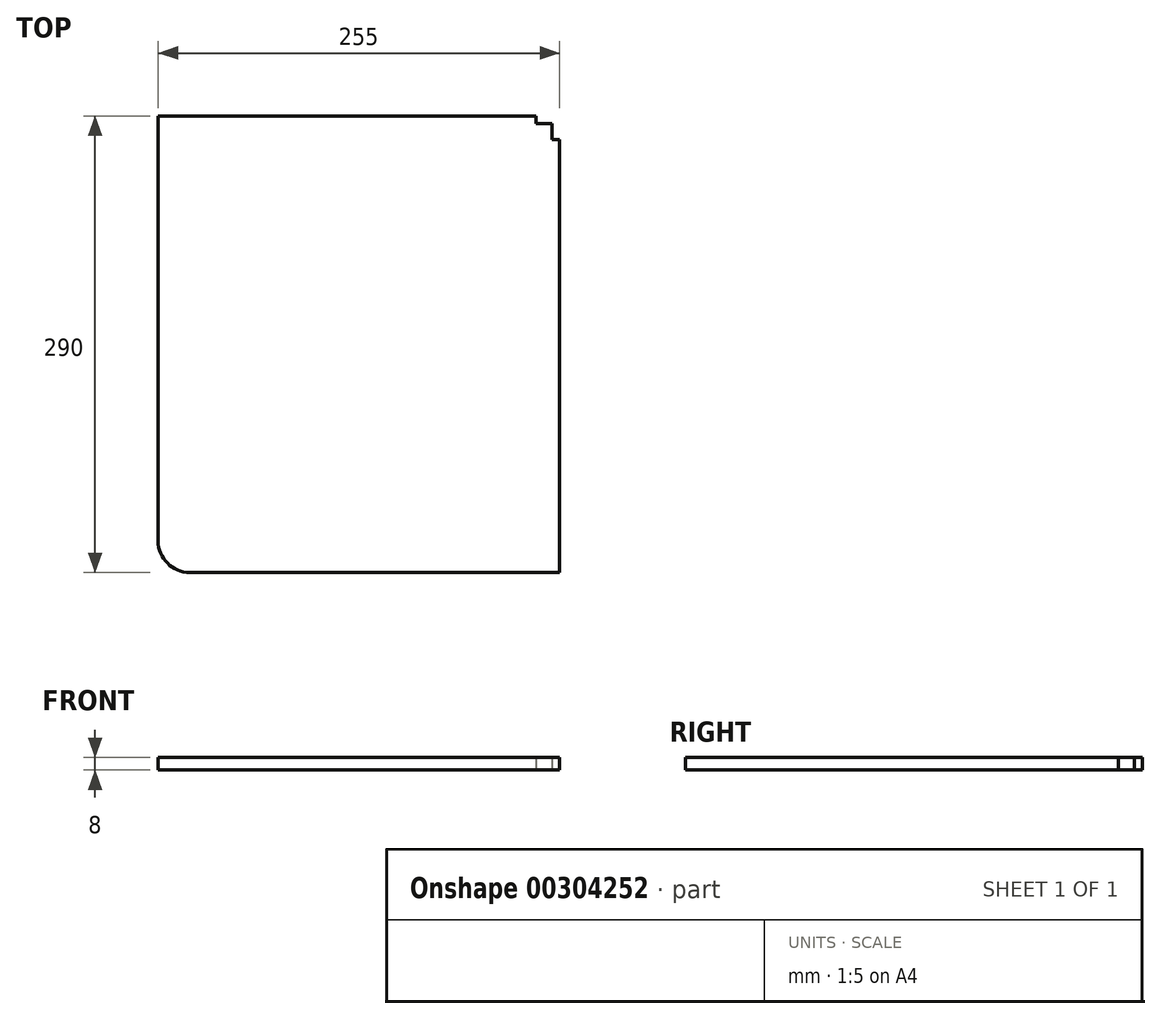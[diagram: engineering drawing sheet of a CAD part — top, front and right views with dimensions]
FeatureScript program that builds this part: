
annotation { "Feature Type Name" : "Feature", "Feature Type Description" : "" }
export const myFeature = defineFeature(function(context is Context, id is Id, definition is map)
    precondition{}
    {
        {
            var Q0;
            Q0=qCreatedBy(makeId("Top.planeOp"),FACE);
            var sketch = newSketch(context, id + "F0", { "sketchPlane" : qUnion([Q0])});
            skLineSegment(sketch, "E0", {"start": v(112.5, 145) * mm, "end": v(-127.5, 145) * mm});
            skLineSegment(sketch, "E1", {"start": v(-127.5, 145) * mm, "end": v(-127.5, -125) * mm});
            skLineSegment(sketch, "E2", {"start": v(-107.5, -145) * mm, "end": v(127.5, -145) * mm});
            skLineSegment(sketch, "E3", {"start": v(127.5, -145) * mm, "end": v(127.5, 130) * mm});
            skLineSegment(sketch, "E4", {"start": v(127.5, 130) * mm, "end": v(122.5, 130) * mm});
            skLineSegment(sketch, "E5", {"start": v(122.5, 130) * mm, "end": v(122.5, 140) * mm});
            skLineSegment(sketch, "E6", {"start": v(122.5, 140) * mm, "end": v(112.5, 140) * mm});
            skLineSegment(sketch, "E7", {"start": v(112.5, 140) * mm, "end": v(112.5, 145) * mm});
            skLineSegment(sketch, "E8", {"start": v(-127.5, 0) * mm, "end": v(127.5, 0) * mm, "construction": true});
            skPoint(sketch, "E9.visualSharp", {"position": v(-127.5, -145) * mm});
            skArc(sketch, "E9.filletArc", {"start": v(-127.5, -125) * mm, "mid": v(-121.64, -139.14) * mm, "end": v(-107.5, -145) * mm});
            skSolve(sketch);
        }
        {
            var Q0;
            Q0 = qSketchRegion(id + "F0", true);
            extrude(context, id + "F1", {"entities" : qUnion([Q0]), "depth" : 8 * mm});
        }
    });
